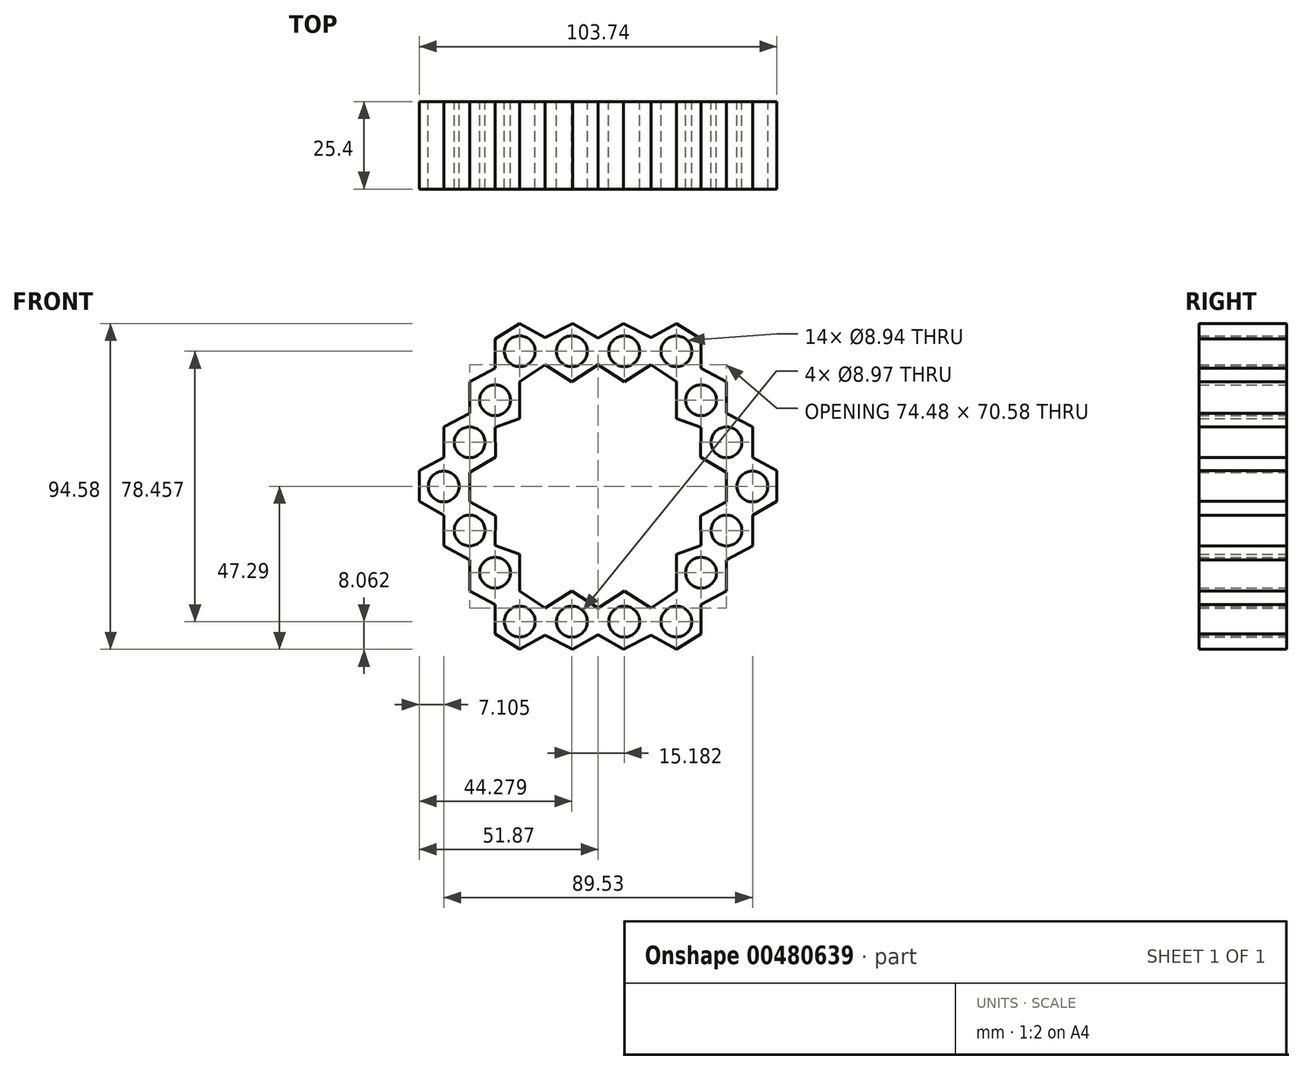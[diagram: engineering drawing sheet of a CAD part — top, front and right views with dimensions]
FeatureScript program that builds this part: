
annotation { "Feature Type Name" : "Feature", "Feature Type Description" : "" }
export const myFeature = defineFeature(function(context is Context, id is Id, definition is map)
    precondition{}
    {
        {
            var Q0;
            Q0=qCreatedBy(makeId("Front.planeOp"),FACE);
            var sketch = newSketch(context, id + "F0", { "sketchPlane" : qUnion([Q0])});
            skLineSegment(sketch, "E0", {"start": v(-29.86, 34.34) * mm, "end": v(-29.86, 42.8) * mm});
            skLineSegment(sketch, "E1", {"start": v(-29.86, 42.8) * mm, "end": v(-22.72, 47.29) * mm});
            skLineSegment(sketch, "E2", {"start": v(-22.72, 47.29) * mm, "end": v(-15.34, 43.17) * mm});
            skLineSegment(sketch, "E3", {"start": v(-15.34, 43.17) * mm, "end": v(-15.34, 35.29) * mm});
            skLineSegment(sketch, "E4", {"start": v(-15.34, 35.29) * mm, "end": v(-22.72, 30.34) * mm});
            skLineSegment(sketch, "E5", {"start": v(-22.72, 30.34) * mm, "end": v(-29.86, 34.34) * mm});
            skLineSegment(sketch, "E6", {"start": v(-15.34, 35.29) * mm, "end": v(-7.6, 30.34) * mm});
            skLineSegment(sketch, "E7", {"start": v(-7.6, 30.34) * mm, "end": v(0, 35.29) * mm});
            skLineSegment(sketch, "E8", {"start": v(0, 35.29) * mm, "end": v(0, 43.05) * mm});
            skLineSegment(sketch, "E9", {"start": v(0, 43.05) * mm, "end": v(-7.35, 47.29) * mm});
            skLineSegment(sketch, "E10", {"start": v(-7.35, 47.29) * mm, "end": v(-15.34, 43.17) * mm});
            skLineSegment(sketch, "E11", {"start": v(-29.86, 34.34) * mm, "end": v(-37.24, 30.34) * mm});
            skLineSegment(sketch, "E12", {"start": v(-37.24, 30.34) * mm, "end": v(-37.24, 21.27) * mm});
            skLineSegment(sketch, "E13", {"start": v(-37.24, 21.27) * mm, "end": v(-29.86, 17.14) * mm});
            skLineSegment(sketch, "E14", {"start": v(-29.86, 17.14) * mm, "end": v(-22.72, 19.7) * mm});
            skLineSegment(sketch, "E15", {"start": v(-22.72, 19.7) * mm, "end": v(-22.72, 30.34) * mm});
            skLineSegment(sketch, "E16", {"start": v(-7.6, 30.34) * mm, "end": v(-7.6, 21.27) * mm});
            skLineSegment(sketch, "E17", {"start": v(-7.6, 21.27) * mm, "end": v(-15.34, 16.23) * mm});
            skLineSegment(sketch, "E18", {"start": v(-15.34, 16.23) * mm, "end": v(-22.72, 19.7) * mm});
            skLineSegment(sketch, "E19", {"start": v(-37.24, 21.27) * mm, "end": v(-44.76, 17.26) * mm});
            skLineSegment(sketch, "E20", {"start": v(-44.76, 17.26) * mm, "end": v(-44.76, 8.34) * mm});
            skLineSegment(sketch, "E21", {"start": v(-44.76, 8.34) * mm, "end": v(-37.24, 4.13) * mm});
            skLineSegment(sketch, "E22", {"start": v(-37.24, 4.13) * mm, "end": v(-29.73, 8.48) * mm});
            skLineSegment(sketch, "E23", {"start": v(-29.73, 8.48) * mm, "end": v(-29.86, 17.14) * mm});
            skLineSegment(sketch, "E24", {"start": v(-15.34, 16.23) * mm, "end": v(-15.34, 7.8) * mm});
            skLineSegment(sketch, "E25", {"start": v(-15.34, 7.8) * mm, "end": v(-22.44, 4.5) * mm});
            skLineSegment(sketch, "E26", {"start": v(-22.44, 4.5) * mm, "end": v(-29.73, 8.48) * mm});
            skLineSegment(sketch, "E27", {"start": v(-7.6, 21.27) * mm, "end": v(0, 17.03) * mm});
            skLineSegment(sketch, "E28", {"start": v(0, 17.03) * mm, "end": v(0, 8.48) * mm});
            skLineSegment(sketch, "E29", {"start": v(0, 8.48) * mm, "end": v(-7.6, 3.54) * mm});
            skLineSegment(sketch, "E30", {"start": v(-7.6, 3.54) * mm, "end": v(-15.34, 7.8) * mm});
            skLineSegment(sketch, "E31", {"start": v(-44.76, 8.34) * mm, "end": v(-51.87, 4.59) * mm});
            skLineSegment(sketch, "E32", {"start": v(-51.87, 4.59) * mm, "end": v(-51.87, -4.37) * mm});
            skLineSegment(sketch, "E33", {"start": v(-51.87, -4.37) * mm, "end": v(-44.76, -8.34) * mm});
            skLineSegment(sketch, "E34", {"start": v(-44.76, -8.34) * mm, "end": v(-37.23, -4.5) * mm});
            skLineSegment(sketch, "E35", {"start": v(-37.23, -4.5) * mm, "end": v(-37.24, 4.13) * mm});
            skLineSegment(sketch, "E36", {"start": v(-22.44, 4.5) * mm, "end": v(-22.44, -4.47) * mm});
            skLineSegment(sketch, "E37", {"start": v(-22.44, -4.47) * mm, "end": v(-29.73, -8.48) * mm});
            skLineSegment(sketch, "E38", {"start": v(-29.73, -8.48) * mm, "end": v(-37.23, -4.5) * mm});
            skLineSegment(sketch, "E39.MirrorCS", {"start": v(-44.76, -17.26) * mm, "end": v(-44.76, -8.34) * mm});
            skLineSegment(sketch, "E40.MirrorCS", {"start": v(-37.24, -21.27) * mm, "end": v(-44.76, -17.26) * mm});
            skLineSegment(sketch, "E41.MirrorCS", {"start": v(-37.24, -21.27) * mm, "end": v(-29.86, -17.14) * mm});
            skLineSegment(sketch, "E42.MirrorCS", {"start": v(-29.73, -8.48) * mm, "end": v(-29.86, -17.14) * mm});
            skLineSegment(sketch, "E43.MirrorCS", {"start": v(-22.44, -4.5) * mm, "end": v(-29.73, -8.48) * mm});
            skLineSegment(sketch, "E44.MirrorCS", {"start": v(-15.34, -7.8) * mm, "end": v(-22.44, -4.5) * mm});
            skLineSegment(sketch, "E45.MirrorCS", {"start": v(-15.34, -16.23) * mm, "end": v(-15.34, -7.8) * mm});
            skLineSegment(sketch, "E46.MirrorCS", {"start": v(-7.6, -21.27) * mm, "end": v(-15.34, -16.23) * mm});
            skLineSegment(sketch, "E47.MirrorCS", {"start": v(-7.6, -21.27) * mm, "end": v(0, -17.03) * mm});
            skLineSegment(sketch, "E48.MirrorCS", {"start": v(0, -17.03) * mm, "end": v(0, -8.48) * mm});
            skLineSegment(sketch, "E49.MirrorCS", {"start": v(0, -8.48) * mm, "end": v(-7.6, -3.54) * mm});
            skLineSegment(sketch, "E50.MirrorCS", {"start": v(-37.24, -30.34) * mm, "end": v(-37.24, -21.27) * mm});
            skLineSegment(sketch, "E51.MirrorCS", {"start": v(-29.86, -34.34) * mm, "end": v(-37.24, -30.34) * mm});
            skLineSegment(sketch, "E52.MirrorCS", {"start": v(-22.72, -30.34) * mm, "end": v(-29.86, -34.34) * mm});
            skLineSegment(sketch, "E53.MirrorCS", {"start": v(-22.72, -19.7) * mm, "end": v(-22.72, -30.34) * mm});
            skLineSegment(sketch, "E54.MirrorCS", {"start": v(-29.86, -17.14) * mm, "end": v(-22.72, -19.7) * mm});
            skLineSegment(sketch, "E55.MirrorCS", {"start": v(-15.34, -16.23) * mm, "end": v(-22.72, -19.7) * mm});
            skLineSegment(sketch, "E56.MirrorCS", {"start": v(-7.6, -3.54) * mm, "end": v(-15.34, -7.8) * mm});
            skLineSegment(sketch, "E57.MirrorCS", {"start": v(-7.6, -30.34) * mm, "end": v(-7.6, -21.27) * mm});
            skLineSegment(sketch, "E58.MirrorCS", {"start": v(-15.34, -35.29) * mm, "end": v(-7.6, -30.34) * mm});
            skLineSegment(sketch, "E59.MirrorCS", {"start": v(-15.34, -43.17) * mm, "end": v(-15.34, -35.29) * mm});
            skLineSegment(sketch, "E60.MirrorCS", {"start": v(-7.35, -47.29) * mm, "end": v(-15.34, -43.17) * mm});
            skLineSegment(sketch, "E61.MirrorCS", {"start": v(0, -43.05) * mm, "end": v(-7.35, -47.29) * mm});
            skLineSegment(sketch, "E62.MirrorCS", {"start": v(-7.6, -30.34) * mm, "end": v(0, -35.29) * mm});
            skLineSegment(sketch, "E63.MirrorCS", {"start": v(-22.72, -47.29) * mm, "end": v(-15.34, -43.17) * mm});
            skLineSegment(sketch, "E64.MirrorCS", {"start": v(-29.86, -42.8) * mm, "end": v(-22.72, -47.29) * mm});
            skLineSegment(sketch, "E65.MirrorCS", {"start": v(-29.86, -34.34) * mm, "end": v(-29.86, -42.8) * mm});
            skLineSegment(sketch, "E66.MirrorCS", {"start": v(-15.34, -35.29) * mm, "end": v(-22.72, -30.34) * mm});
            skLineSegment(sketch, "E67.MirrorCS", {"start": v(7.6, 30.34) * mm, "end": v(0, 35.29) * mm});
            skLineSegment(sketch, "E68.MirrorCS", {"start": v(0, 43.05) * mm, "end": v(7.35, 47.29) * mm});
            skLineSegment(sketch, "E69.MirrorCS", {"start": v(7.35, 47.29) * mm, "end": v(15.34, 43.17) * mm});
            skLineSegment(sketch, "E70.MirrorCS", {"start": v(15.34, 35.29) * mm, "end": v(7.6, 30.34) * mm});
            skLineSegment(sketch, "E71.MirrorCS", {"start": v(7.6, 30.34) * mm, "end": v(7.6, 21.27) * mm});
            skLineSegment(sketch, "E72.MirrorCS", {"start": v(7.6, 21.27) * mm, "end": v(0, 17.03) * mm});
            skLineSegment(sketch, "E73.MirrorCS", {"start": v(0, 8.48) * mm, "end": v(7.6, 3.54) * mm});
            skLineSegment(sketch, "E74.MirrorCS", {"start": v(7.6, -21.27) * mm, "end": v(0, -17.03) * mm});
            skLineSegment(sketch, "E75.MirrorCS", {"start": v(7.6, -30.34) * mm, "end": v(0, -35.29) * mm});
            skLineSegment(sketch, "E76.MirrorCS", {"start": v(0, -43.05) * mm, "end": v(7.35, -47.29) * mm});
            skLineSegment(sketch, "E77.MirrorCS", {"start": v(7.35, -47.29) * mm, "end": v(15.34, -43.17) * mm});
            skLineSegment(sketch, "E78.MirrorCS", {"start": v(22.72, -47.29) * mm, "end": v(15.34, -43.17) * mm});
            skLineSegment(sketch, "E79.MirrorCS", {"start": v(29.86, -42.8) * mm, "end": v(22.72, -47.29) * mm});
            skLineSegment(sketch, "E80.MirrorCS", {"start": v(29.86, -34.34) * mm, "end": v(29.86, -42.8) * mm});
            skLineSegment(sketch, "E81.MirrorCS", {"start": v(22.72, -30.34) * mm, "end": v(29.86, -34.34) * mm});
            skLineSegment(sketch, "E82.MirrorCS", {"start": v(15.34, -35.29) * mm, "end": v(22.72, -30.34) * mm});
            skLineSegment(sketch, "E83.MirrorCS", {"start": v(22.72, -19.7) * mm, "end": v(22.72, -30.34) * mm});
            skLineSegment(sketch, "E84.MirrorCS", {"start": v(15.34, -16.23) * mm, "end": v(22.72, -19.7) * mm});
            skLineSegment(sketch, "E85.MirrorCS", {"start": v(29.86, -17.14) * mm, "end": v(22.72, -19.7) * mm});
            skLineSegment(sketch, "E86.MirrorCS", {"start": v(29.86, -34.34) * mm, "end": v(37.24, -30.34) * mm});
            skLineSegment(sketch, "E87.MirrorCS", {"start": v(37.24, -30.34) * mm, "end": v(37.24, -21.27) * mm});
            skLineSegment(sketch, "E88.MirrorCS", {"start": v(37.24, -21.27) * mm, "end": v(44.76, -17.26) * mm});
            skLineSegment(sketch, "E89.MirrorCS", {"start": v(37.24, -21.27) * mm, "end": v(29.86, -17.14) * mm});
            skLineSegment(sketch, "E90.MirrorCS", {"start": v(29.73, -8.48) * mm, "end": v(29.86, -17.14) * mm});
            skLineSegment(sketch, "E91.MirrorCS", {"start": v(29.73, -8.48) * mm, "end": v(37.23, -4.5) * mm});
            skLineSegment(sketch, "E92.MirrorCS", {"start": v(44.76, -8.34) * mm, "end": v(37.23, -4.5) * mm});
            skLineSegment(sketch, "E93.MirrorCS", {"start": v(51.87, -4.37) * mm, "end": v(44.76, -8.34) * mm});
            skLineSegment(sketch, "E94.MirrorCS", {"start": v(51.87, 4.59) * mm, "end": v(51.87, -4.37) * mm});
            skLineSegment(sketch, "E95.MirrorCS", {"start": v(44.76, -17.26) * mm, "end": v(44.76, -8.34) * mm});
            skLineSegment(sketch, "E96.MirrorCS", {"start": v(44.76, 8.34) * mm, "end": v(37.24, 4.13) * mm});
            skLineSegment(sketch, "E97.MirrorCS", {"start": v(44.76, 17.26) * mm, "end": v(44.76, 8.34) * mm});
            skLineSegment(sketch, "E98.MirrorCS", {"start": v(37.24, 21.27) * mm, "end": v(44.76, 17.26) * mm});
            skLineSegment(sketch, "E99.MirrorCS", {"start": v(29.73, 8.48) * mm, "end": v(29.86, 17.14) * mm});
            skLineSegment(sketch, "E100.MirrorCS", {"start": v(37.24, 21.27) * mm, "end": v(29.86, 17.14) * mm});
            skLineSegment(sketch, "E101.MirrorCS", {"start": v(37.24, 30.34) * mm, "end": v(37.24, 21.27) * mm});
            skLineSegment(sketch, "E102.MirrorCS", {"start": v(29.86, 34.34) * mm, "end": v(37.24, 30.34) * mm});
            skLineSegment(sketch, "E103.MirrorCS", {"start": v(29.86, 34.34) * mm, "end": v(29.86, 42.8) * mm});
            skLineSegment(sketch, "E104.MirrorCS", {"start": v(29.86, 42.8) * mm, "end": v(22.72, 47.29) * mm});
            skLineSegment(sketch, "E105.MirrorCS", {"start": v(22.72, 47.29) * mm, "end": v(15.34, 43.17) * mm});
            skLineSegment(sketch, "E106.MirrorCS", {"start": v(15.34, 43.17) * mm, "end": v(15.34, 35.29) * mm});
            skLineSegment(sketch, "E107.MirrorCS", {"start": v(15.34, 16.23) * mm, "end": v(15.34, 7.8) * mm});
            skLineSegment(sketch, "E108.MirrorCS", {"start": v(29.86, 17.14) * mm, "end": v(22.72, 19.7) * mm});
            skLineSegment(sketch, "E109.MirrorCS", {"start": v(15.34, 16.23) * mm, "end": v(22.72, 19.7) * mm});
            skLineSegment(sketch, "E110.MirrorCS", {"start": v(15.34, 7.8) * mm, "end": v(22.44, 4.5) * mm});
            skLineSegment(sketch, "E111.MirrorCS", {"start": v(22.44, 4.5) * mm, "end": v(29.73, 8.48) * mm});
            skLineSegment(sketch, "E112.MirrorCS", {"start": v(22.44, 4.5) * mm, "end": v(22.44, -4.47) * mm});
            skLineSegment(sketch, "E113.MirrorCS", {"start": v(22.44, -4.47) * mm, "end": v(29.73, -8.48) * mm});
            skLineSegment(sketch, "E114.MirrorCS", {"start": v(37.23, -4.5) * mm, "end": v(37.24, 4.13) * mm});
            skLineSegment(sketch, "E115.MirrorCS", {"start": v(7.6, -21.27) * mm, "end": v(15.34, -16.23) * mm});
            skLineSegment(sketch, "E116.MirrorCS", {"start": v(7.6, -30.34) * mm, "end": v(7.6, -21.27) * mm});
            skLineSegment(sketch, "E117.MirrorCS", {"start": v(0, -8.48) * mm, "end": v(7.6, -3.54) * mm});
            skLineSegment(sketch, "E118.MirrorCS", {"start": v(7.6, -3.54) * mm, "end": v(15.34, -7.8) * mm});
            skLineSegment(sketch, "E119.MirrorCS", {"start": v(15.34, 35.29) * mm, "end": v(22.72, 30.34) * mm});
            skLineSegment(sketch, "E120.MirrorCS", {"start": v(22.72, 30.34) * mm, "end": v(29.86, 34.34) * mm});
            skLineSegment(sketch, "E121.MirrorCS", {"start": v(7.6, 21.27) * mm, "end": v(15.34, 16.23) * mm});
            skLineSegment(sketch, "E122.MirrorCS", {"start": v(7.6, 3.54) * mm, "end": v(15.34, 7.8) * mm});
            skLineSegment(sketch, "E123", {"start": v(-7.6, 3.54) * mm, "end": v(-7.6, -3.54) * mm});
            skLineSegment(sketch, "E124", {"start": v(7.6, 3.54) * mm, "end": v(7.6, -3.54) * mm});
            skLineSegment(sketch, "E125.MirrorCS", {"start": v(15.34, -16.23) * mm, "end": v(15.34, -7.8) * mm});
            skLineSegment(sketch, "E126.MirrorCS", {"start": v(15.34, -7.8) * mm, "end": v(22.44, -4.5) * mm});
            skLineSegment(sketch, "E127.MirrorCS", {"start": v(44.76, 8.34) * mm, "end": v(51.87, 4.59) * mm});
            skLineSegment(sketch, "E128.MirrorCS", {"start": v(15.34, -43.17) * mm, "end": v(15.34, -35.29) * mm});
            skLineSegment(sketch, "E129.MirrorCS", {"start": v(15.34, -35.29) * mm, "end": v(7.6, -30.34) * mm});
            skLineSegment(sketch, "E130", {"start": v(0, -43.05) * mm, "end": v(0, -35.29) * mm});
            skLineSegment(sketch, "E131.MirrorCS", {"start": v(37.24, 4.13) * mm, "end": v(29.73, 8.48) * mm});
            skLineSegment(sketch, "E132.MirrorCS", {"start": v(22.72, 19.7) * mm, "end": v(22.72, 30.34) * mm});
            skCircle(sketch, "E133", {"center": v(-22.72, 39.23) * mm, "radius": 4.47 * mm});
            skPoint(sketch, "E133.centerSnap0", {"position": v(-15.34, 39.23) * mm});
            skCircle(sketch, "E134", {"center": v(-7.6, 39.23) * mm, "radius": 4.49 * mm});
            skCircle(sketch, "E135", {"center": v(-29.86, 25.02) * mm, "radius": 4.47 * mm});
            skPoint(sketch, "E135.centerSnap0", {"position": v(-22.72, 25.02) * mm});
            skCircle(sketch, "E136", {"center": v(-15.34, 25.02) * mm, "radius": 4.47 * mm});
            skCircle(sketch, "E137", {"center": v(0, 25.8) * mm, "radius": 4.47 * mm});
            skPoint(sketch, "E137.centerSnap0", {"position": v(-7.6, 25.8) * mm});
            skCircle(sketch, "E138", {"center": v(-37.24, 12.8) * mm, "radius": 4.47 * mm});
            skPoint(sketch, "E138.centerSnap0", {"position": v(-44.76, 12.8) * mm});
            skCircle(sketch, "E139", {"center": v(-22.44, 12.81) * mm, "radius": 4.47 * mm});
            skPoint(sketch, "E139.centerSnap0", {"position": v(-29.8, 12.81) * mm});
            skCircle(sketch, "E140", {"center": v(-7.6, 12.01) * mm, "radius": 4.47 * mm});
            skPoint(sketch, "E140.centerSnap0", {"position": v(-15.34, 12.01) * mm});
            skCircle(sketch, "E141", {"center": v(-44.76, 0) * mm, "radius": 4.47 * mm});
            skCircle(sketch, "E142", {"center": v(-29.73, 0) * mm, "radius": 4.47 * mm});
            skCircle(sketch, "E143", {"center": v(-15.34, 0) * mm, "radius": 4.47 * mm});
            skCircle(sketch, "E144.MirrorC", {"center": v(22.72, 39.23) * mm, "radius": 4.47 * mm});
            skCircle(sketch, "E145.MirrorC", {"center": v(7.6, 39.23) * mm, "radius": 4.49 * mm});
            skCircle(sketch, "E146.MirrorC", {"center": v(15.34, 25.02) * mm, "radius": 4.47 * mm});
            skCircle(sketch, "E147.MirrorC", {"center": v(29.86, 25.02) * mm, "radius": 4.47 * mm});
            skCircle(sketch, "E148.MirrorC", {"center": v(37.24, 12.8) * mm, "radius": 4.47 * mm});
            skCircle(sketch, "E149.MirrorC", {"center": v(22.44, 12.81) * mm, "radius": 4.47 * mm});
            skCircle(sketch, "E150.MirrorC", {"center": v(7.6, 12.01) * mm, "radius": 4.47 * mm});
            skCircle(sketch, "E151.MirrorC", {"center": v(15.34, 0) * mm, "radius": 4.47 * mm});
            skCircle(sketch, "E152.MirrorC", {"center": v(29.73, 0) * mm, "radius": 4.47 * mm});
            skCircle(sketch, "E153.MirrorC", {"center": v(44.76, 0) * mm, "radius": 4.47 * mm});
            skCircle(sketch, "E154.MirrorC", {"center": v(-7.6, -12.01) * mm, "radius": 4.47 * mm});
            skCircle(sketch, "E155.MirrorC", {"center": v(-22.44, -12.81) * mm, "radius": 4.47 * mm});
            skCircle(sketch, "E156.MirrorC", {"center": v(-37.24, -12.8) * mm, "radius": 4.47 * mm});
            skCircle(sketch, "E157.MirrorC", {"center": v(-15.34, -25.02) * mm, "radius": 4.47 * mm});
            skCircle(sketch, "E158.MirrorC", {"center": v(-29.86, -25.02) * mm, "radius": 4.47 * mm});
            skCircle(sketch, "E159.MirrorC", {"center": v(-22.72, -39.23) * mm, "radius": 4.47 * mm});
            skCircle(sketch, "E160.MirrorC", {"center": v(-7.6, -39.23) * mm, "radius": 4.49 * mm});
            skCircle(sketch, "E161.MirrorC", {"center": v(7.6, -39.23) * mm, "radius": 4.49 * mm});
            skCircle(sketch, "E162.MirrorC", {"center": v(22.72, -39.23) * mm, "radius": 4.47 * mm});
            skCircle(sketch, "E163.MirrorC", {"center": v(15.34, -25.02) * mm, "radius": 4.47 * mm});
            skCircle(sketch, "E164.MirrorC", {"center": v(29.86, -25.02) * mm, "radius": 4.47 * mm});
            skCircle(sketch, "E165.MirrorC", {"center": v(22.44, -12.81) * mm, "radius": 4.47 * mm});
            skCircle(sketch, "E166.MirrorC", {"center": v(37.24, -12.8) * mm, "radius": 4.47 * mm});
            skCircle(sketch, "E167.MirrorC", {"center": v(7.6, -12.01) * mm, "radius": 4.47 * mm});
            skCircle(sketch, "E168.MirrorC", {"center": v(0, -25.8) * mm, "radius": 4.47 * mm});
            skCircle(sketch, "E169", {"center": v(0, 0) * mm, "radius": 4.47 * mm});
            skSolve(sketch);
        }
        {
            var Q0;
            Q0 = qSketchRegion(id + "F0", true);
            extrude(context, id + "F1", {"entities" : qUnion([Q0]), "depth" : 25.4 * mm});
        }
    });
